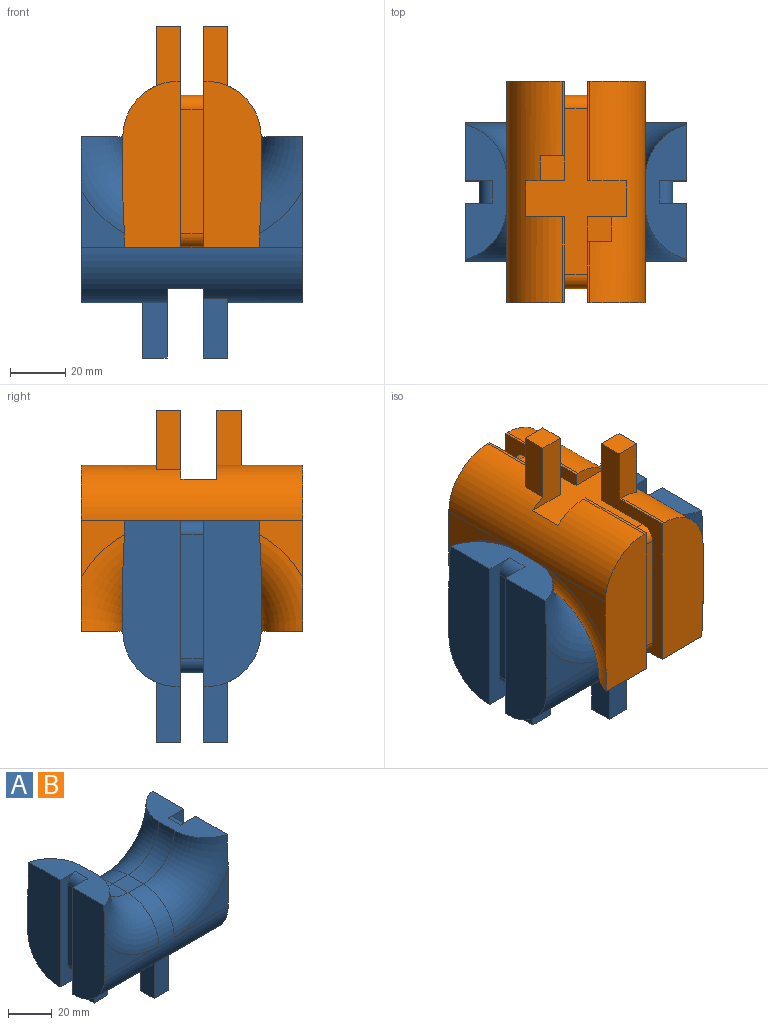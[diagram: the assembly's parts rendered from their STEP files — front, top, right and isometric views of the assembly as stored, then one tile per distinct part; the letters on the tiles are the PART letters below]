
ASSEMBLY  parts=2 mates=1
PART A: 44 faces, bbox 127.3x50x80 mm
  f0: plane 22x1mm, normal (0,0,-1), area 22mm2, adj f13,f20,f24,f40
  f1: plane 27x1mm, normal (0,0,-1), area 27mm2, adj f2,f9,f28,f38
  f2: plane 60x21mm, normal (1,0,0), area 1167.8mm2, adj f1,f3,f9,f17,f22,f28
  f3: plane 48.73x15mm, normal (0,0,1), area 500.4mm2, adj f2,f8,f14,f19,f22,f27,f28,f35
  f4: plane 60x21mm, normal (-1,0,0), area 1167.8mm2, adj f7,f9,f10,f12,f23,f31
  f5: plane 60x36.46mm, normal (0,0,-1), area 849.9mm2, adj f9,f20,f24,f25,f26,f27,f28,f29
  f6: plane 36x1mm, normal (0,0,-1), area 36mm2, adj f8,f20,f26,f27
  f7: plane 31x1mm, normal (0,0,-1), area 31mm2, adj f4,f9,f30,f31
  f8: plane 60x21mm, normal (1,0,0), area 1167.8mm2, adj f3,f6,f11,f19,f20,f27
  f9: cylinder r=20mm len=80mm, axis (1,0,0), area 2565.4mm2, adj f1,f2,f4,f5,f7,f10,f15,f17
  f10: plane 35x20.64mm, normal (0,-1,0), area 208.8mm2, adj f4,f9,f23
  f11: plane 35x20.64mm, normal (0,1,0), area 208.8mm2, adj f8,f19,f20
  f12: plane 48.73x15mm, normal (0,0,1), area 500.4mm2, adj f4,f13,f16,f21,f23,f24,f31,f37
  f13: plane 60x21mm, normal (-1,0,0), area 1167.8mm2, adj f0,f12,f18,f20,f21,f24
  f14: cylinder r=20mm len=20mm, axis (0,1,0), area 314.2mm2, adj f3,f15,f19,f22
  f15: plane 10x10mm, normal (0,0,1), area 100mm2, adj f9,f14,f16,f20
  f16: cylinder r=20mm len=20mm, axis (0,1,0), area 314.2mm2, adj f12,f15,f21,f23
  f17: plane 35x20.64mm, normal (0,-1,0), area 208.8mm2, adj f2,f9,f22
  f18: plane 35x20.64mm, normal (0,1,0), area 208.8mm2, adj f13,f20,f21
  f19: torus R=40mm, axis (0,-1,0), area 1279.7mm2, adj f3,f8,f11,f14,f20
  f20: cylinder r=20mm len=80mm, axis (-1,0,0), area 2565.4mm2, adj f0,f5,f6,f8,f11,f13,f15,f18
  f21: torus R=40mm, axis (0,-1,0), area 1279.7mm2, adj f12,f13,f16,f18,f20
  f22: torus R=40mm, axis (0,-1,0), area 1279.7mm2, adj f2,f3,f9,f14,f17
  f23: torus R=40mm, axis (0,-1,0), area 1279.7mm2, adj f4,f9,f10,f12,f16
  f24: plane 80x31mm, normal (0,-1,0), area 620.7mm2, adj f0,f5,f12,f13,f25,f32,f36,f37
  f25: plane 25x14.23mm, normal (1,0,0), area 234.7mm2, adj f5,f20,f24,f41,f43
  f26: plane 14.23x5mm, normal (-1,0,0), area 50.3mm2, adj f5,f6,f20,f27
  f27: plane 60x36mm, normal (0,-1,0), area 465.7mm2, adj f3,f5,f6,f8,f26,f33,f34,f35
  f28: plane 80x36mm, normal (0,1,0), area 645.7mm2, adj f1,f2,f3,f5,f29,f33,f34,f35
  f29: plane 25x14.23mm, normal (-1,0,0), area 234.7mm2, adj f5,f9,f28,f39,f42
  f30: plane 14.23x5mm, normal (1,0,0), area 50.3mm2, adj f5,f7,f9,f31
  f31: plane 60x31mm, normal (0,1,0), area 440.7mm2, adj f4,f5,f7,f12,f30,f32,f36,f37
  f32: plane 45x8mm, normal (-1,0,0), area 360mm2, adj f24,f31,f36,f37
  f33: plane 45x8mm, normal (1,0,0), area 360mm2, adj f27,f28,f34,f35
  f34: cylinder r=5mm len=8mm, axis (0,1,0), area 62.8mm2, adj f5,f27,f28,f33
  f35: cylinder r=5mm len=8mm, axis (0,1,0), area 62.8mm2, adj f3,f27,f28,f33
  f36: cylinder r=5mm len=8mm, axis (0,1,0), area 62.8mm2, adj f5,f24,f31,f32
  f37: cylinder r=5mm len=8mm, axis (0,-1,0), area 62.8mm2, adj f12,f24,f31,f32
  f38: plane 21.67x9mm, normal (1,0,0), area 184.4mm2, adj f1,f9,f28,f39,f42
  f39: plane 21.67x9mm, normal (0,-1,0), area 195mm2, adj f9,f29,f38,f42
  f40: plane 21.67x9mm, normal (-1,0,0), area 184.4mm2, adj f0,f20,f24,f41,f43
  f41: plane 21.67x9mm, normal (0,1,0), area 195mm2, adj f20,f25,f40,f43
  f42: plane 9x9mm, normal (0,0,-1), area 81mm2, adj f28,f29,f38,f39
  f43: plane 9x9mm, normal (0,0,-1), area 81mm2, adj f24,f25,f40,f41
PART B: same geometry as A
PLACE A t=(-34,0,-97.5)mm
PLACE B rot(axis=(0.71,0.71,0),180deg) t=(144.57,-178.57,-35.02)mm
MATE revolute B.f20 <-> A.f14  axis (0,-1,0) through (124.57,-25,-46.26)mm
